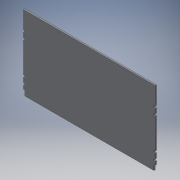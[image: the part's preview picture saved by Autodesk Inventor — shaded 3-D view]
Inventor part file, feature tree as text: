
AUTODESK INVENTOR PART (.ipt)
format: ipt  version: 2019 (Build 230136000, 136)  size: 183,808 bytes
history: native  units: in
note: dims shown in document units (in); Inventor stores cm internally (conversion verified against a paired STEP export)
features: reference x14, extrude x3, sketch x3, other x3, helix x1
ambient origin geometry x8: Origin, YZ Plane, XZ Plane, XY Plane, X Axis, Y Axis, Z Axis, Center Point
bodies: Solid1 (feature_tree)
feature tree (24):
  extrude  "Extrusion1"  Depth=9.0551in
  extrude  "Extrusion4"  Depth=0.5906in
  extrude  "Extrusion5"  Depth=0.0039in
  sketch  "Sketch1"  dims[d0=15.748in d1=9.0551in]
  sketch  "Sketch4"  dims[d2=0.1575in d3=0.0in d31=0.5906in]
  reference  "Reference1"
  reference  "Reference2"
  sketch  "Sketch5"  dims[d50=0.3937in d51=0.0in d52=0.1181in d53=0.1181in d54=0.1181in d55=0.1181in d56=0.3937in d57=0.0in d58=0.0039in d59=0.0039in d60=0.0039in d61=0.0039in d62=0.0039in d63=0.0039in d64=0.0039in d65=0.0039in]
  reference  "Reference3"
  reference  "Reference4"
  reference  "Reference5"
  reference  "Reference6"
  reference  "Reference7"
  reference  "Reference8"
  reference  "Reference9"
  reference  "Reference10"
  reference  "Reference11"
  reference  "Reference12"
  reference  "Reference13"
  reference  "Reference14"
  other  "<userpath>\Documents\CAD Files\Helix DLP\Helix DLP Z Stage.iam"
  helix  "Helix DLP Z Stage.iam"  [1 undecoded]
  other  "Z stage_side:2"
  other  "Z stage_side:1"
note: 1 required parameter value undecoded (feature->parameter linkage not recoverable at this tier; creation-order binding heuristic only, values carry confidence <= 0.55)
